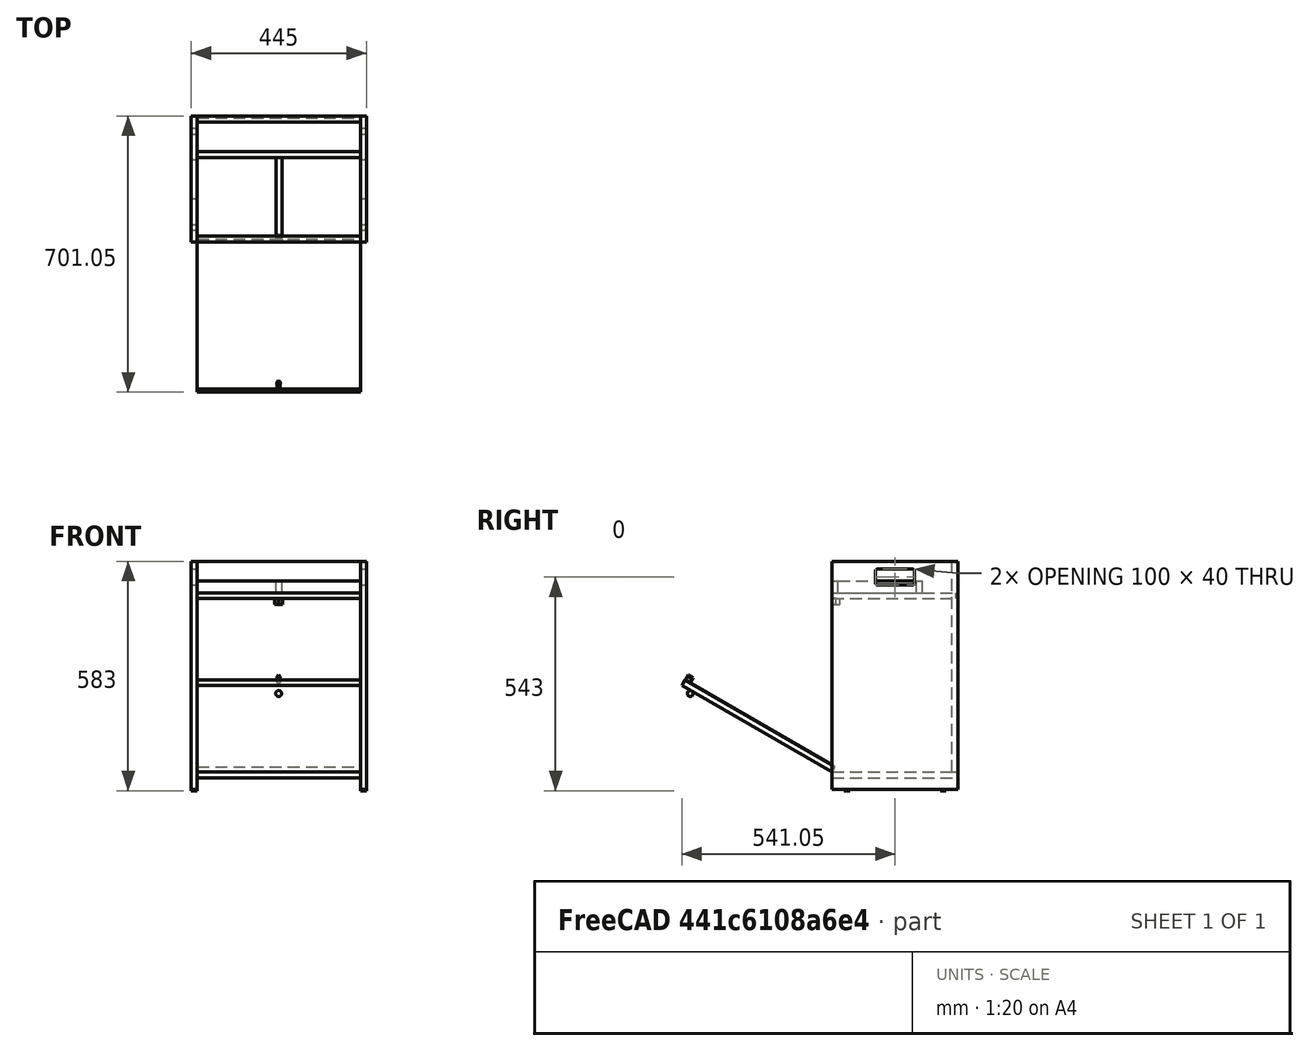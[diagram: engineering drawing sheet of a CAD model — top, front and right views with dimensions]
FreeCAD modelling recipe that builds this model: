
FCSTD DOCUMENT  (FreeCAD 0.17R13522 (Git))
Label: SuporteParaComedouroTamanho3
License: All rights reserved
LicenseURL: http://en.wikipedia.org/wiki/All_rights_reserved
objects: Part::Box×17, Part::Cylinder×4, Part::Cut×4, Part::Fillet×2, Part::Sphere×1, Part::MultiFuse×1, Part::Chamfer×1
note: 30 computed .brp shape members not serialized (recipe doc carries the construction recipe); baked Part::Feature solids carry a one-line shape summary decoded from their .brp

FEATURE [Part::Box] Box  label="SuporteFrenteSuperiorVertical"
  AttacherType = Attacher::AttachEngine3D
  Height = 30
  Length = 415
  Placement = pos=(0,0,150) rot=(0,0,1;0rad)
  Width = 15
FEATURE [Part::Box] Box001  label="SuporteLateralVerticalEsquerdo"
  AttacherType = Attacher::AttachEngine3D
  Height = 580
  Length = 15
  Placement = pos=(-15,0,-350) rot=(0,0,1;0rad)
  Width = 320
FEATURE [Part::Box] Box002  label="SuporteLateralVerticalDireito"
  AttacherType = Attacher::AttachEngine3D
  Height = 580
  Length = 15
  Placement = pos=(415,0,-350) rot=(0,0,1;0rad)
  Width = 320
FEATURE [Part::Box] Box003  label="TampoSuperiorHorizontal"
  AttacherType = Attacher::AttachEngine3D
  Height = 15
  Length = 415
  Placement = pos=(0,0,135) rot=(0,0,1;0rad)
  Width = 315
FEATURE [Part::Box] Box004  label="SuporteFundoVertical"
  AttacherType = Attacher::AttachEngine3D
  Height = 535
  Length = 415
  Placement = pos=(0,305,-305) rot=(0,0,1;0rad)
  Width = 15
FEATURE [Part::Box] Box005  label="SuporteVerticalMeio"
  AttacherType = Attacher::AttachEngine3D
  Height = 30
  Length = 15
  Placement = pos=(200,15,150) rot=(0,0,1;0rad)
  Width = 200
FEATURE [Part::Box] Box006  label="TampoInferiorHorizontal"
  AttacherType = Attacher::AttachEngine3D
  Height = 15
  Length = 415
  Placement = pos=(0,0,-320) rot=(0,0,1;0rad)
  Width = 320
FEATURE [Part::Box] Box007  label="Cube"
  AttacherType = Attacher::AttachEngine3D
  Height = 3
  Length = 15
  Placement = pos=(-15,30,-353) rot=(0,0,1;0rad)
  Width = 15
FEATURE [Part::Box] Box008  label="Cube001"
  AttacherType = Attacher::AttachEngine3D
  Height = 3
  Length = 15
  Placement = pos=(-15,275,-353) rot=(0,0,1;0rad)
  Width = 15
FEATURE [Part::Box] Box009  label="Cube002"
  AttacherType = Attacher::AttachEngine3D
  Height = 3
  Length = 15
  Placement = pos=(415,30,-353) rot=(0,0,1;0rad)
  Width = 15
FEATURE [Part::Box] Box010  label="Cube003"
  AttacherType = Attacher::AttachEngine3D
  Height = 3
  Length = 15
  Placement = pos=(415,275,-353) rot=(0,0,1;0rad)
  Width = 15
FEATURE [Part::Box] Box011  label="TampaBasculante"
  AttacherType = Attacher::AttachEngine3D
  Height = 440
  Length = 415
  Placement = pos=(0,0,-305) rot=(1,0,0;1.0472rad)
  Width = 15
FEATURE [Part::Sphere] Sphere  label="Puxador"
  Angle1 = -90
  Angle2 = 90
  Angle3 = 360
  AttacherType = Attacher::AttachEngine3D
  Placement = pos=(207,-360,-106) rot=(0,0,1;0rad)
  Radius = 7.5
FEATURE [Part::Cylinder] Cylinder
  Angle = 360
  AttacherType = Attacher::AttachEngine3D
  Height = 15
  Placement = pos=(-100,0,0) rot=(0,0,1;0rad)
  Radius = 5
FEATURE [Part::Cylinder] Cylinder001
  Angle = 360
  AttacherType = Attacher::AttachEngine3D
  Height = 15
  Placement = pos=(-90,0,0) rot=(0,0,1;0rad)
  Radius = 5
FEATURE [Part::Box] Box012  label="Cube004"
  AttacherType = Attacher::AttachEngine3D
  Height = 15
  Length = 10
  Placement = pos=(-100,5,0) rot=(0,0,1;0rad)
  Width = 10
FEATURE [Part::MultiFuse] Fusion
  Placement = pos=(302,5,120) rot=(0,0,1;0rad)
  Shapes = -> [Cylinder,Cylinder001,Box012]
FEATURE [Part::Box] Box013  label="Cube005"
  AttacherType = Attacher::AttachEngine3D
  Height = 15
  Length = 8
  Placement = pos=(193,-130,-70) rot=(0,0,1;0rad)
  Width = 15
FEATURE [Part::Chamfer] Chamfer
  Base = -> Box013
  Edges = 2 edges r=3.9: [Edge3,Edge7]
FEATURE [Part::Cylinder] Cylinder002
  Angle = 360
  AttacherType = Attacher::AttachEngine3D
  Height = 15
  Placement = pos=(212,-124,-70) rot=(0,0,1;0rad)
  Radius = 12
FEATURE [Part::Cylinder] Cylinder003
  Angle = 360
  AttacherType = Attacher::AttachEngine3D
  Height = 15
  Placement = pos=(182,-124,-70) rot=(0,0,1;0rad)
  Radius = 12
FEATURE [Part::Cut] Cut
  Base = -> Chamfer
  Tool = -> Cylinder002
FEATURE [Part::Cut] Cut001
  Base = -> Cut
  Placement = pos=(10,-356,68) rot=(1,0,0;1.0472rad)
  Tool = -> Cylinder003
FEATURE [Part::Box] Box014  label="Cube006"
  AttacherType = Attacher::AttachEngine3D
  Height = 40
  Length = 15
  Placement = pos=(-67,110,170) rot=(0,0,1;0rad)
  Width = 100
FEATURE [Part::Box] Box015  label="SuporteFrenteSuperiorVertical001"
  AttacherType = Attacher::AttachEngine3D
  Height = 30
  Length = 415
  Placement = pos=(0,215,150) rot=(0,0,1;0rad)
  Width = 15
FEATURE [Part::Fillet] Fillet
  Base = -> Box014
  Edges = 4 edges r=5: [Edge9,Edge10,Edge11,Edge12]
  Placement = pos=(52,0,0) rot=(0,0,1;0rad)
FEATURE [Part::Box] Box016  label="Cube007"
  AttacherType = Attacher::AttachEngine3D
  Height = 40
  Length = 15
  Placement = pos=(-67,110,170) rot=(0,0,1;0rad)
  Width = 100
FEATURE [Part::Fillet] Fillet001
  Base = -> Box016
  Edges = 4 edges r=5: [Edge9,Edge10,Edge11,Edge12]
  Placement = pos=(482,0,0) rot=(0,0,1;0rad)
FEATURE [Part::Cut] Cut002
  Base = -> Box002
  Tool = -> Fillet001
FEATURE [Part::Cut] Cut003
  Base = -> Box001
  Tool = -> Fillet
